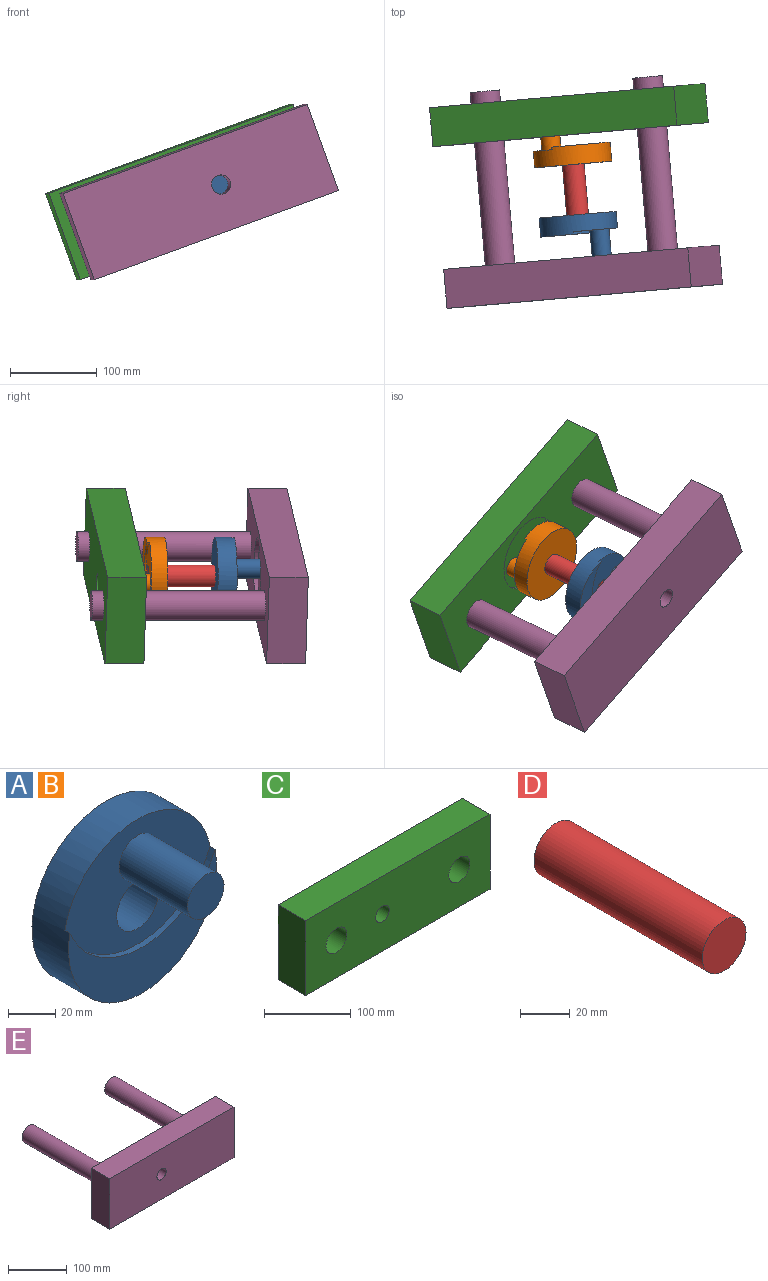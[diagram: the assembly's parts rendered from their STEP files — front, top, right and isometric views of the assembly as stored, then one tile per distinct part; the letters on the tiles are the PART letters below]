
ASSEMBLY  parts=5 mates=4
PART A: 8 faces, bbox 88.9x60x88.9 mm
  f0: cylinder r=44.45mm len=88.9mm, axis (0,-1,0), area 5776.3mm2, adj f1,f2,f3,f4
  f1: plane 88.9x88.9mm, normal (0,1,0), area 5716.3mm2, adj f0,f7
  f2: plane 88.9x52.88mm, normal (0,-1,0), area 2017.7mm2, adj f0,f3
  f3: cylinder r=47.32mm len=87.29mm, axis (0,-1,0), area 333.3mm2, adj f0,f2,f4
  f4: plane 87.29x65.05mm, normal (0,-1,0), area 3318.5mm2, adj f0,f3,f6,f7
  f5: plane 22x22mm, normal (0,-1,0), area 380.1mm2, adj f6
  f6: cylinder r=11mm len=41mm, axis (0,1,0), area 2833.7mm2, adj f4,f5
  f7: cylinder r=12.5mm len=25mm, axis (0,-1,0), area 1492.3mm2, adj f1,f4
PART B: same geometry as A
PART C: 11 faces, bbox 300x45x105.6 mm
  f0: plane 300x45mm, normal (0,0,1), area 13500mm2, adj f1,f3,f4,f5
  f1: plane 105.58x45mm, normal (-1,0,0), area 4751.1mm2, adj f0,f2,f4,f5
  f2: plane 300x45mm, normal (0,0,-1), area 13500mm2, adj f1,f3,f4,f5
  f3: plane 105.58x45mm, normal (1,0,0), area 4751.1mm2, adj f0,f2,f4,f5
  f4: plane 300x105.58mm, normal (0,-1,0), area 29474.6mm2, adj f0,f1,f2,f3,f8,f9,f10
  f5: plane 300x105.58mm, normal (0,1,0), area 23637.1mm2, adj f0,f1,f2,f3,f6,f9,f10
  f6: cylinder r=44.5mm len=89mm, axis (0,1,0), area 1398mm2, adj f5,f7
  f7: plane 89x89mm, normal (0,1,0), area 5837.5mm2, adj f6,f8
  f8: cylinder r=11.05mm len=40mm, axis (0,1,0), area 2777.2mm2, adj f4,f7
  f9: cylinder r=17mm len=45mm, axis (0,1,0), area 4806.6mm2, adj f4,f5
  f10: cylinder r=17mm len=45mm, axis (0,1,0), area 4806.6mm2, adj f4,f5
PART D: 3 faces, bbox 25x96x25 mm
  f0: cylinder r=12.5mm len=96mm, axis (0,1,0), area 7539.8mm2, adj f1,f2
  f1: plane 25x25mm, normal (0,-1,0), area 490.9mm2, adj f0
  f2: plane 25x25mm, normal (0,1,0), area 490.9mm2, adj f0
PART E: 13 faces, bbox 300x245x105.6 mm
  f0: plane 300x45mm, normal (0,0,1), area 13500mm2, adj f1,f3,f4,f5
  f1: plane 105.58x45mm, normal (-1,0,0), area 4751.1mm2, adj f0,f2,f4,f5
  f2: plane 300x45mm, normal (0,0,-1), area 13500mm2, adj f1,f3,f4,f5
  f3: plane 105.58x45mm, normal (1,0,0), area 4751.1mm2, adj f0,f2,f4,f5
  f4: plane 300x105.58mm, normal (0,-1,0), area 31290.5mm2, adj f0,f1,f2,f3,f8
  f5: plane 300x105.58mm, normal (0,1,0), area 23637.1mm2, adj f0,f1,f2,f3,f6,f9,f11
  f6: cylinder r=44.5mm len=89mm, axis (0,1,0), area 1398mm2, adj f5,f7
  f7: plane 89x89mm, normal (0,1,0), area 5837.5mm2, adj f6,f8
  f8: cylinder r=11.05mm len=40mm, axis (0,1,0), area 2777.2mm2, adj f4,f7
  f9: cylinder r=17mm len=200mm, axis (0,-1,0), area 21362.8mm2, adj f5,f10
  f10: plane 34x34mm, normal (0,1,0), area 907.9mm2, adj f9
  f11: cylinder r=17mm len=200mm, axis (0,-1,0), area 21362.8mm2, adj f5,f12
  f12: plane 34x34mm, normal (0,1,0), area 907.9mm2, adj f11
PLACE A rot(axis=(-0.04,1,0.06),70.2deg) t=(10.91,-131.76,-20.72)mm
PLACE B rot(axis=(0.82,0.04,-0.57),177.1deg) t=(2.02,-30.15,-20.72)mm
PLACE C rot(axis=(-0.98,-0.04,-0.17),179.1deg) t=(0.93,-17.7,-20.72)mm
PLACE D rot(axis=(0.82,0.04,-0.57),177.1deg) t=(10.65,-128.78,-20.72)mm
PLACE E rot(axis=(-0.04,1,0.01),160deg) t=(13.28,-158.82,-20.72)mm fixed
MATE revolute C.f8 <-> B.f6  axis (0.09,-1,0) through (-22.9,-14.77,-29.27)mm
MATE slider E.f9 <-> C.f9  axis (0.09,-1,0) through (-89.05,-67.39,-54.92)mm
MATE fastened D.f0 <-> B.f0  axis (0.09,-1,0) through (2.29,-33.14,-20.72)mm
MATE fastened D.f0 <-> A.f0  axis (0.09,-1,0) through (10.65,-128.78,-20.72)mm
